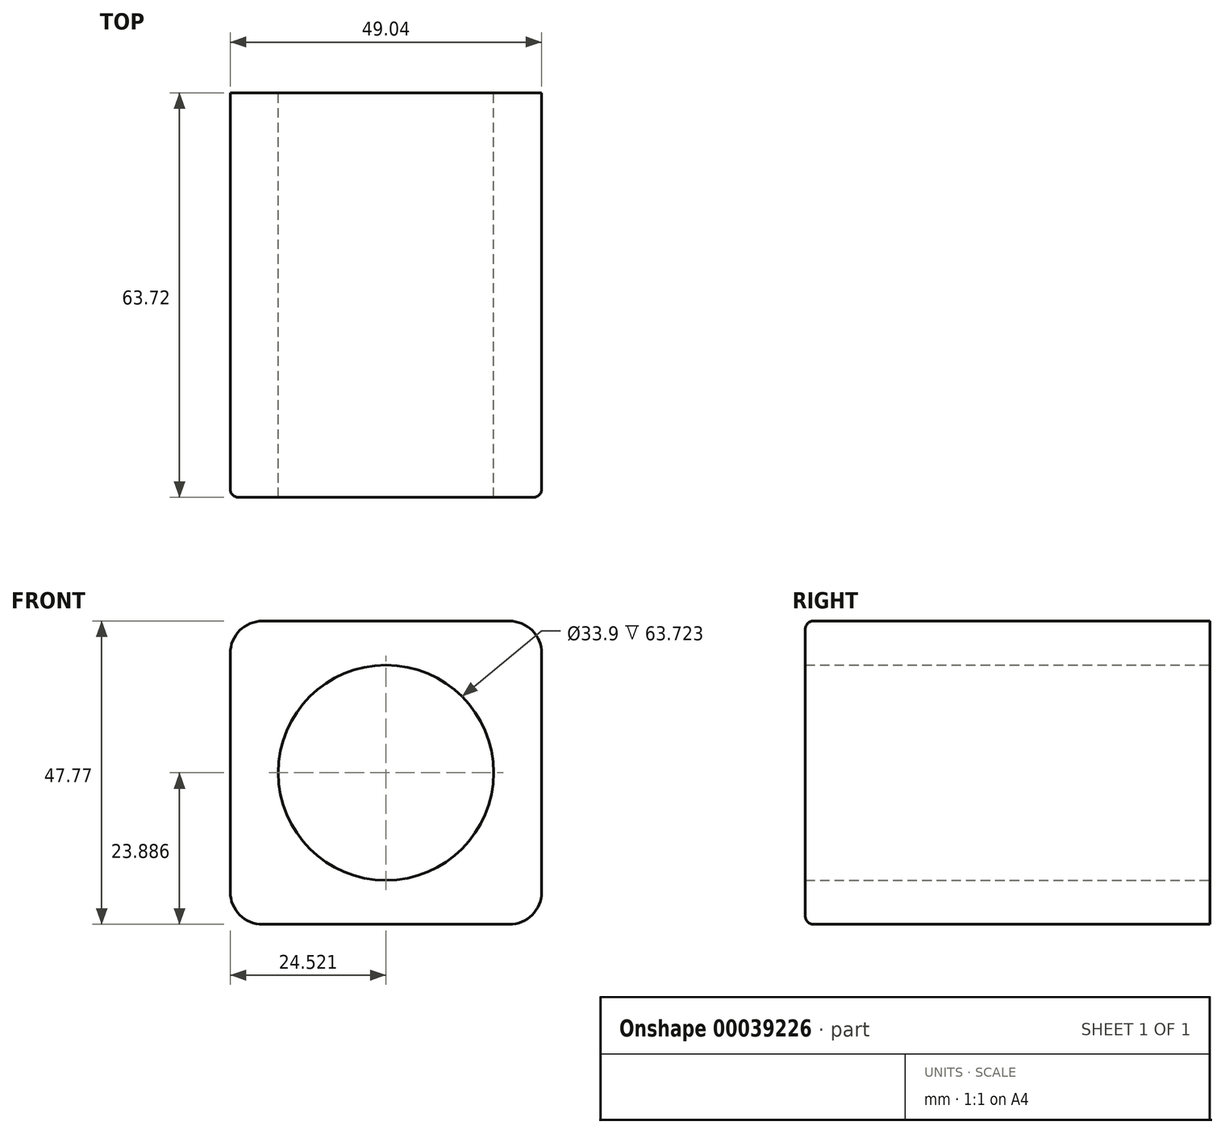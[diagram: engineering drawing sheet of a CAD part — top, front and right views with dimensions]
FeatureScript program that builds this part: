
annotation { "Feature Type Name" : "Feature", "Feature Type Description" : "" }
export const myFeature = defineFeature(function(context is Context, id is Id, definition is map)
    precondition{}
    {
        {
            var Q0;
            Q0=qCreatedBy(makeId("Front.planeOp"),FACE);
            var sketch = newSketch(context, id + "F0", { "sketchPlane" : qUnion([Q0])});
            skLineSegment(sketch, "E0.bottom", {"start": v(0, 0) * mm, "end": v(49.04, 0) * mm});
            skLineSegment(sketch, "E0.top", {"start": v(0, 47.77) * mm, "end": v(49.04, 47.77) * mm});
            skLineSegment(sketch, "E0.left", {"start": v(0, 0) * mm, "end": v(0, 47.77) * mm});
            skLineSegment(sketch, "E0.right", {"start": v(49.04, 0) * mm, "end": v(49.04, 47.77) * mm});
            skCircle(sketch, "E1", {"center": v(24.52, 23.89) * mm, "radius": 16.95 * mm});
            skPoint(sketch, "E1.centerSnap0", {"position": v(24.52, 47.77) * mm});
            skPoint(sketch, "E1.centerSnap1", {"position": v(0, 23.89) * mm});
            skSolve(sketch);
        }
        {
            var Q0;
            Q0=makeQuery(id+"F0.imprint","IMPRINT",FACE,{"disambiguationData":[TD([[makeQuery(id+"F0.imprint","IMPRINT",EDGE,{"derivedFrom":sQuery(id+"F0.wireOp",EDGE,"E0.bottom")}),1.0]])]});
            extrude(context, id + "F1", {"entities" : qUnion([Q0]), "depth" : 63.72 * mm});
        }
        {
            var Q0;
            Q0=makeQuery(id+"F1.opExtrude","SWEPT_EDGE",EDGE,{"disambiguationData":[OSD([sQuery(id+"F0.wireOp",EDGE,"E0.top"),sQuery(id+"F0.wireOp",EDGE,"E0.right")])]});
            var Q1;
            Q1=makeQuery(id+"F1.opExtrude","SWEPT_EDGE",EDGE,{"disambiguationData":[OSD([sQuery(id+"F0.wireOp",EDGE,"E0.top"),sQuery(id+"F0.wireOp",EDGE,"E0.left")])]});
            var Q2;
            Q2=makeQuery(id+"F1.opExtrude","SWEPT_EDGE",EDGE,{"disambiguationData":[OSD([sQuery(id+"F0.wireOp",EDGE,"E0.bottom"),sQuery(id+"F0.wireOp",EDGE,"E0.right")])]});
            var Q3;
            Q3=makeQuery(id+"F1.opExtrude","SWEPT_EDGE",EDGE,{"disambiguationData":[OSD([sQuery(id+"F0.wireOp",EDGE,"E0.bottom"),sQuery(id+"F0.wireOp",EDGE,"E0.left")])]});
            fillet(context, id + "F2", {"entities" : qUnion([Q0, Q1, Q2, Q3]), "radius" : 5.08 * mm, "tangentPropagation" : true, "allowEdgeOverflow" : false});
        }
        {
            var Q0;
            Q0=makeQuery(id+"F1.opExtrude","CAP_EDGE",EDGE,{"disambiguationData":[OSD([sQuery(id+"F0.wireOp",EDGE,"E0.right")])],"isStart":false});
            fillet(context, id + "F3", {"entities" : qUnion([Q0]), "radius" : 1.27 * mm, "tangentPropagation" : true, "allowEdgeOverflow" : false});
        }
    });
